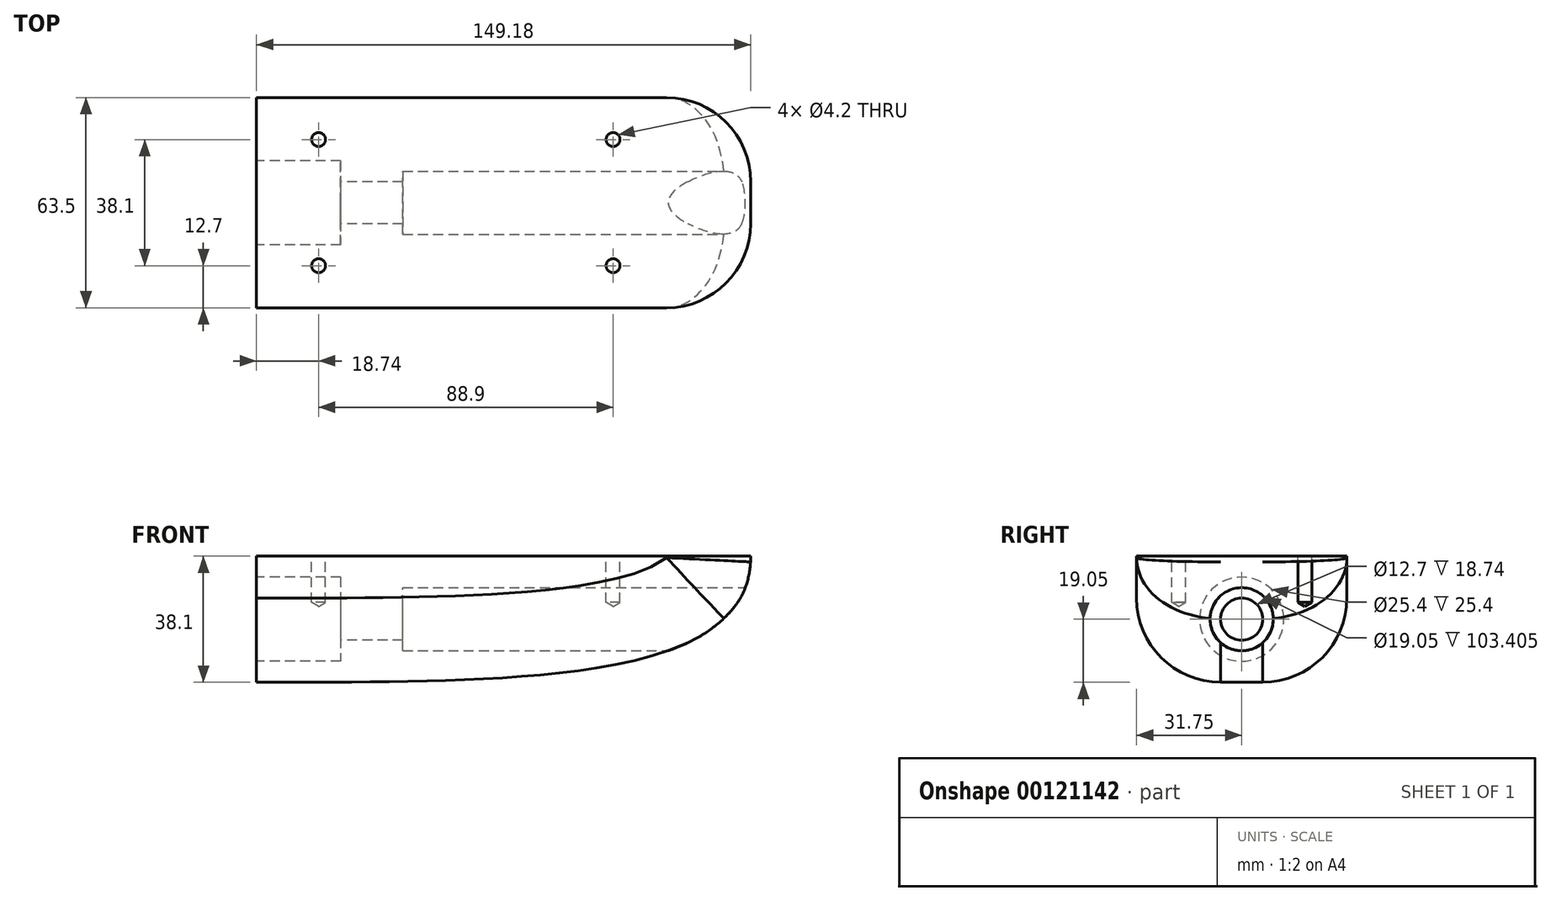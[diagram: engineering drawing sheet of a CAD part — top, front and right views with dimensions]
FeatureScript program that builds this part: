
annotation { "Feature Type Name" : "Feature", "Feature Type Description" : "" }
export const myFeature = defineFeature(function(context is Context, id is Id, definition is map)
    precondition{}
    {
        {
            var Q0;
            Q0=qCreatedBy(makeId("Front.planeOp"),FACE);
            var sketch = newSketch(context, id + "F0", { "sketchPlane" : qUnion([Q0])});
            skPoint(sketch, "E0.middle", {"position": v(0, 0) * mm});
            skLineSegment(sketch, "E1", {"start": v(-82.24, 19.05) * mm, "end": v(66.94, 19.05) * mm});
            skLineSegment(sketch, "E2", {"start": v(-82.24, 19.05) * mm, "end": v(-82.24, -19.05) * mm});
            skFitSpline(sketch, "E3", {"points": [v(-82.24, -19.05) * mm, v(66.94, 19.05) * mm], "startDerivative": vector(246.72, 0) * mm, "endDerivative": vector(0, 114.3) * mm});
            skSolve(sketch);
        }
        {
            var Q0;
            Q0 = qSketchRegion(id + "F0", true);
            extrude(context, id + "F1", {"entities" : qUnion([Q0]), "depth" : 31.75 * mm, "hasSecondDirection" : true, "secondDirectionOppositeDirection" : true, "secondDirectionDepth" : 31.75 * mm});
        }
        {
            var Q0;
            Q0=makeQuery(id+"F1.opExtrude","CAP_EDGE",EDGE,{"disambiguationData":[OSD([sQuery(id+"F0.wireOp",EDGE,"E3")])],"isStart":false});
            var Q1;
            Q1=makeQuery(id+"F1.opExtrude","CAP_EDGE",EDGE,{"disambiguationData":[OSD([sQuery(id+"F0.wireOp",EDGE,"E3")])],"isStart":true});
            fillet(context, id + "F2", {"entities" : qUnion([Q0, Q1]), "radius" : 25.4 * mm, "tangentPropagation" : true, "allowEdgeOverflow" : false});
        }
        {
            var Q0;
            Q0=makeQuery(id+"F1.opExtrude","SWEPT_FACE",FACE,{"disambiguationData":[OSD([sQuery(id+"F0.wireOp",EDGE,"E2")])]});
            var sketch = newSketch(context, id + "F3", { "sketchPlane" : qUnion([Q0])});
            skCircle(sketch, "E4", {"center": v(0, 0) * mm, "radius": 6.35 * mm});
            skSolve(sketch);
        }
        {
            var Q0;
            Q0 = qSketchRegion(id + "F3", true);
            extrude(context, id + "F4", {"entities" : qUnion([Q0]), "operationType" : NewBodyOperationType.REMOVE, "endBound" : BoundingType.THROUGH_ALL, "oppositeDirection" : true, "depth" : 25.4 * mm});
        }
        {
            var Q0;
            Q0=makeQuery(id+"F1.opExtrude","SWEPT_FACE",FACE,{"disambiguationData":[OSD([sQuery(id+"F0.wireOp",EDGE,"E2")])]});
            var sketch = newSketch(context, id + "F5", { "sketchPlane" : qUnion([Q0])});
            skCircle(sketch, "E5", {"center": v(0, 0) * mm, "radius": 12.7 * mm});
            skSolve(sketch);
        }
        {
            var Q0;
            Q0 = qSketchRegion(id + "F5", true);
            extrude(context, id + "F6", {"entities" : qUnion([Q0]), "operationType" : NewBodyOperationType.REMOVE, "oppositeDirection" : true, "depth" : 25.4 * mm});
        }
        {
            var Q0;
            Q0=qCreatedBy(makeId("Right.planeOp"),FACE);
            var sketch = newSketch(context, id + "F7", { "sketchPlane" : qUnion([Q0])});
            skCircle(sketch, "E6", {"center": v(0, 0) * mm, "radius": 9.53 * mm});
            skSolve(sketch);
        }
        {
            var Q0;
            Q0 = qSketchRegion(id + "F7", true);
            extrude(context, id + "F8", {"entities" : qUnion([Q0]), "operationType" : NewBodyOperationType.REMOVE, "oppositeDirection" : true, "depth" : 38.1 * mm, "hasSecondDirection" : true, "secondDirectionBound" : SecondDirectionBoundingType.THROUGH_ALL, "secondDirectionOppositeDirection" : false, "secondDirectionDepth" : 25.4 * mm, "offsetDistance" : 25.4 * mm});
        }
        {
            var Q0;
            Q0=makeQuery(id+"F1.opExtrude","SWEPT_FACE",FACE,{"disambiguationData":[OSD([sQuery(id+"F0.wireOp",EDGE,"E1")])]});
            var sketch = newSketch(context, id + "F9", { "sketchPlane" : qUnion([Q0])});
            skPoint(sketch, "E7", {"position": v(-63.5, 19.05) * mm});
            skPoint(sketch, "E8", {"position": v(-63.5, -19.05) * mm});
            skPoint(sketch, "E9", {"position": v(25.4, -19.05) * mm});
            skPoint(sketch, "E10", {"position": v(25.4, 19.05) * mm});
            skSolve(sketch);
        }
        {
            var Q0;
            Q0=sQuery(id+"F9.wireOp",VERTEX,"E7");
            var Q1;
            Q1=sQuery(id+"F9.wireOp",VERTEX,"E8");
            var Q2;
            Q2=sQuery(id+"F9.wireOp",VERTEX,"E10");
            var Q3;
            Q3=sQuery(id+"F9.wireOp",VERTEX,"E9");
            var Q4;
            Q4=makeQuery(id+"F1.opExtrude","SWEPT_BODY",BODY,{"disambiguationData":[OSD([sQuery(id+"F0.wireOp",EDGE,"E1"),sQuery(id+"F0.wireOp",EDGE,"E2"),sQuery(id+"F0.wireOp",EDGE,"E3")])]});
            hole(context, id + "F10", {"style" : HoleStyle.SIMPLE, "endStyle" : HoleEndStyle.BLIND, "standardTappedOrClearance" : lookupTablePath({ "standard" : "ISO", "engagement" : "75%", "pitch" : "0.8 mm", "size" : "M5", "type" : "Tapped" }), "standardBlindInLast" : lookupTablePath({ "standard" : "ISO", "engagement" : "75%", "pitch" : "0.8 mm", "size" : "M5", "type" : "Tapped" }), "holeDiameter" : 4.2 * mm, "holeDepth" : 14 * mm, "startFromSketch" : true, "locations" : qUnion([Q0, Q1, Q2, Q3]), "scope" : qUnion([Q4]), "majorDiameter" : 5 * mm});
        }
    });
